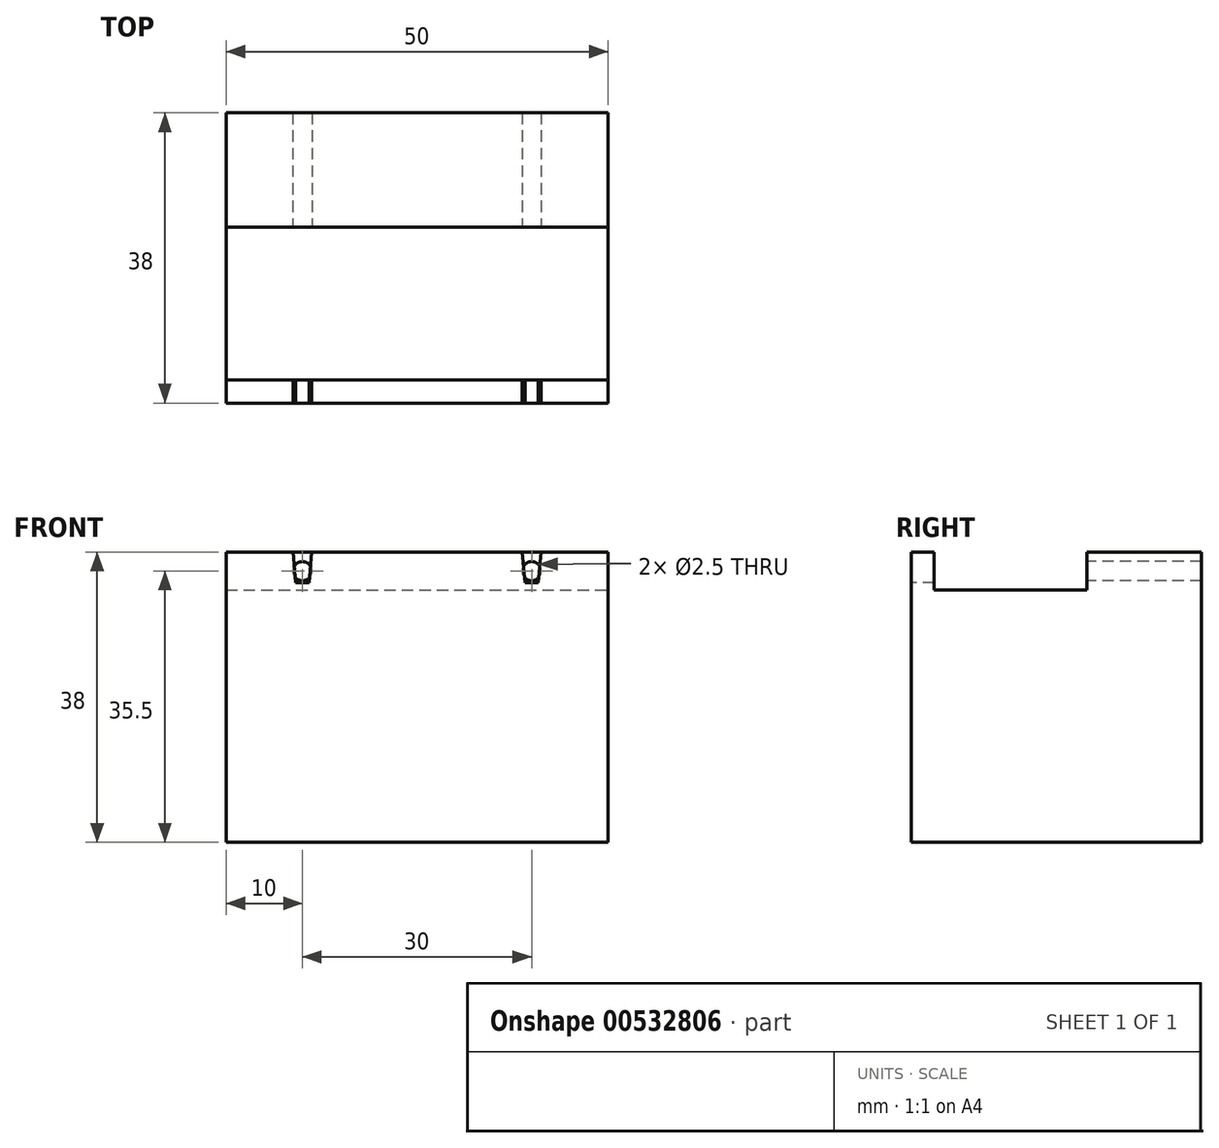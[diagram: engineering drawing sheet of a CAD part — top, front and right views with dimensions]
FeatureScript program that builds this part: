
annotation { "Feature Type Name" : "Feature", "Feature Type Description" : "" }
export const myFeature = defineFeature(function(context is Context, id is Id, definition is map)
    precondition{}
    {
        {
            var Q0;
            Q0=qCreatedBy(makeId("Top.planeOp"),FACE);
            var sketch = newSketch(context, id + "F0", { "sketchPlane" : qUnion([Q0])});
            skLineSegment(sketch, "E0.bottom", {"start": v(0, 0) * mm, "end": v(50, 0) * mm});
            skLineSegment(sketch, "E0.top", {"start": v(0, -38) * mm, "end": v(50, -38) * mm});
            skLineSegment(sketch, "E0.left", {"start": v(0, 0) * mm, "end": v(0, -38) * mm});
            skLineSegment(sketch, "E0.right", {"start": v(50, 0) * mm, "end": v(50, -38) * mm});
            skSolve(sketch);
        }
        {
            var Q0;
            Q0 = qSketchRegion(id + "F0", true);
            extrude(context, id + "F1", {"entities" : qUnion([Q0]), "depth" : 38 * mm, "offsetDistance" : 25 * mm});
        }
        {
            var Q0;
            Q0=makeQuery(id+"F1.opExtrude","CAP_FACE",FACE,{"disambiguationData":[OSD([sQuery(id+"F0.wireOp",EDGE,"E0.bottom"),sQuery(id+"F0.wireOp",EDGE,"E0.top"),sQuery(id+"F0.wireOp",EDGE,"E0.left"),sQuery(id+"F0.wireOp",EDGE,"E0.right")])],"isStart":false});
            var sketch = newSketch(context, id + "F2", { "sketchPlane" : qUnion([Q0])});
            skLineSegment(sketch, "E1.bottom", {"start": v(0, -15) * mm, "end": v(50, -15) * mm});
            skLineSegment(sketch, "E1.top", {"start": v(0, -35) * mm, "end": v(50, -35) * mm});
            skLineSegment(sketch, "E1.left", {"start": v(0, -15) * mm, "end": v(0, -35) * mm});
            skLineSegment(sketch, "E1.right", {"start": v(50, -15) * mm, "end": v(50, -35) * mm});
            skSolve(sketch);
        }
        {
            var Q0;
            Q0=makeQuery(id+"F2.imprint","IMPRINT",FACE,{"disambiguationData":[TD([[makeQuery(id+"F2.imprint","IMPRINT",EDGE,{"derivedFrom":sQuery(id+"F2.wireOp",EDGE,"E1.bottom")}),-1.0]])]});
            extrude(context, id + "F3", {"entities" : qUnion([Q0]), "operationType" : NewBodyOperationType.REMOVE, "oppositeDirection" : true, "depth" : 5 * mm, "offsetDistance" : 25 * mm});
        }
        {
            var Q0;
            Q0=makeQuery(id+"F3.boolean.opBoolean","COPY",FACE,{"derivedFrom":makeQuery(id+"F3.opExtrude","SWEPT_FACE",FACE,{"disambiguationData":[OSD([sQuery(id+"F2.wireOp",EDGE,"E1.bottom")])]})});
            var sketch = newSketch(context, id + "F4", { "sketchPlane" : qUnion([Q0])});
            skCircle(sketch, "E2", {"center": v(10, 35.5) * mm, "radius": 1.25 * mm});
            skCircle(sketch, "E3", {"center": v(40, 35.5) * mm, "radius": 1.25 * mm});
            skSolve(sketch);
        }
        {
            var Q0;
            Q0 = qSketchRegion(id + "F4", true);
            extrude(context, id + "F5", {"entities" : qUnion([Q0]), "operationType" : NewBodyOperationType.REMOVE, "oppositeDirection" : true, "depth" : 25 * mm, "offsetDistance" : 25 * mm});
        }
        {
            var Q0;
            Q0=makeQuery(id+"F1.opExtrude","SWEPT_FACE",FACE,{"disambiguationData":[OSD([sQuery(id+"F0.wireOp",EDGE,"E0.top")])]});
            var sketch = newSketch(context, id + "F6", { "sketchPlane" : qUnion([Q0])});
            skLineSegment(sketch, "E4.bottom", {"start": v(8.78, 38) * mm, "end": v(11.22, 38) * mm});
            skLineSegment(sketch, "E4.top", {"start": v(9.13, 34) * mm, "end": v(10.88, 34) * mm});
            skLineSegment(sketch, "E4.left", {"start": v(8.78, 38) * mm, "end": v(9.13, 34) * mm});
            skLineSegment(sketch, "E4.right", {"start": v(11.22, 38) * mm, "end": v(10.88, 34) * mm});
            skLineSegment(sketch, "E5.bottom", {"start": v(38.78, 38) * mm, "end": v(41.22, 38) * mm});
            skLineSegment(sketch, "E5.top", {"start": v(39.12, 34) * mm, "end": v(40.88, 34) * mm});
            skLineSegment(sketch, "E5.left", {"start": v(38.78, 38) * mm, "end": v(39.12, 34) * mm});
            skLineSegment(sketch, "E5.right", {"start": v(41.22, 38) * mm, "end": v(40.88, 34) * mm});
            skSolve(sketch);
        }
        {
            var Q0;
            Q0=makeQuery(id+"F6.imprint","IMPRINT",FACE,{"disambiguationData":[TD([[makeQuery(id+"F6.imprint","IMPRINT",EDGE,{"derivedFrom":sQuery(id+"F6.wireOp",EDGE,"E4.bottom")}),-1.0]])]});
            var Q1;
            Q1=makeQuery(id+"F6.imprint","IMPRINT",FACE,{"disambiguationData":[TD([[makeQuery(id+"F6.imprint","IMPRINT",EDGE,{"derivedFrom":sQuery(id+"F6.wireOp",EDGE,"E5.bottom")}),-1.0]])]});
            extrude(context, id + "F7", {"entities" : qUnion([Q0, Q1]), "operationType" : NewBodyOperationType.REMOVE, "oppositeDirection" : true, "depth" : 5 * mm, "offsetDistance" : 25 * mm});
        }
    });
